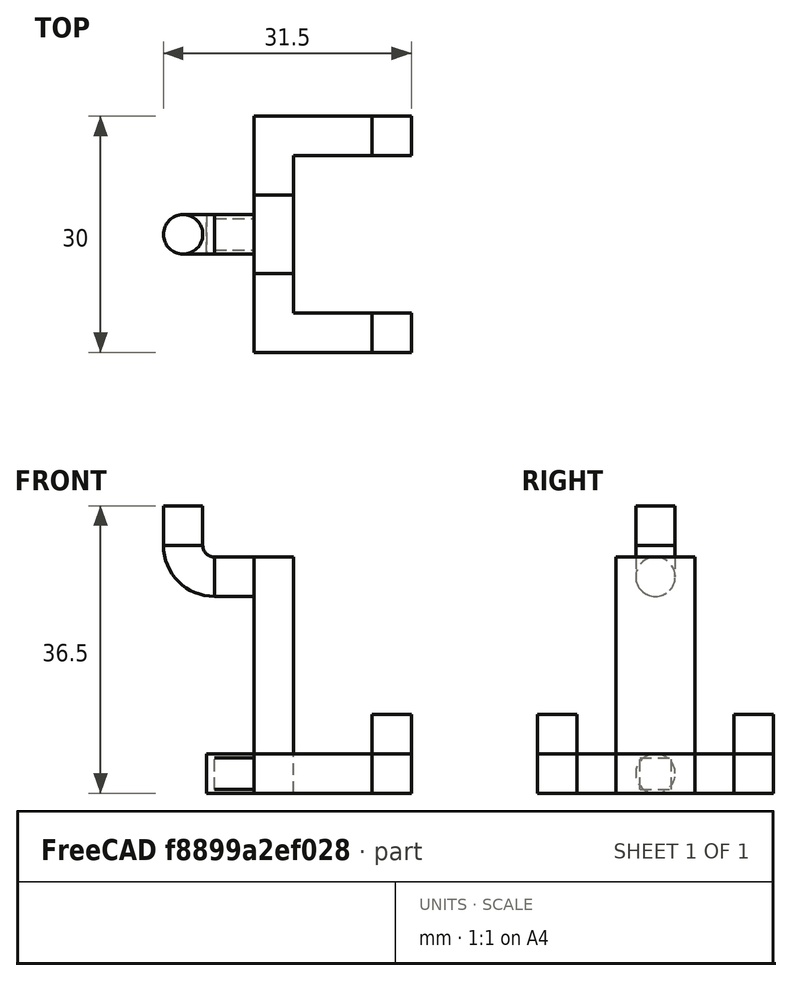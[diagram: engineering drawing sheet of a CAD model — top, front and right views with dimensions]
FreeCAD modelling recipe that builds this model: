
FCSTD DOCUMENT  (FreeCAD 0.17R13522 (Git))
Label: bigscrewdriver
License: All rights reserved
LicenseURL: http://en.wikipedia.org/wiki/All_rights_reserved
objects: Part::Box×6, Part::Cylinder×3, Part::Torus×1, Part::Cut×1
note: 11 computed .brp shape members not serialized (recipe doc carries the construction recipe); baked Part::Feature solids carry a one-line shape summary decoded from their .brp

FEATURE [Part::Cylinder] Cylinder002
  Angle = 360
  AttacherType = Attacher::AttachEngine3D
  Height = 6
  Placement = pos=(-5,0,2.5) rot=(0,-1,0;1.5708rad)
  Radius = 2.5
FEATURE [Part::Box] Box001  label="Cube001"
  AttacherType = Attacher::AttachEngine3D
  Height = 30
  Length = 5
  Placement = pos=(-5,-5,0) rot=(0,0,1;0rad)
  Width = 10
FEATURE [Part::Cylinder] Cylinder003
  Angle = 360
  AttacherType = Attacher::AttachEngine3D
  Height = 5
  Placement = pos=(-5,0,27.5) rot=(0,-1,0;1.5708rad)
  Radius = 2.5
FEATURE [Part::Torus] Torus
  Angle1 = -180
  Angle2 = 180
  Angle3 = 90
  AttacherType = Attacher::AttachEngine3D
  Placement = pos=(-10,0,31.5) rot=(0.57735,-0.57735,-0.57735;4.18879rad)
  Radius1 = 4
  Radius2 = 2.5
FEATURE [Part::Cylinder] Cylinder004
  Angle = 360
  AttacherType = Attacher::AttachEngine3D
  Height = 5
  Placement = pos=(-14,0,31.5) rot=(0,0,1;0rad)
  Radius = 2.5
FEATURE [Part::Box] Box002  label="Cube002"
  AttacherType = Attacher::AttachEngine3D
  Height = 4
  Length = 5
  Placement = pos=(-10,-2,0.5) rot=(0,0,1;0rad)
  Width = 4
FEATURE [Part::Box] Box  label="Cube"
  AttacherType = Attacher::AttachEngine3D
  Height = 5
  Length = 20
  Placement = pos=(-5,-15,0) rot=(0,0,1;0rad)
  Width = 30
FEATURE [Part::Box] Box003  label="Cube003"
  AttacherType = Attacher::AttachEngine3D
  Height = 10
  Length = 15
  Placement = pos=(0,-10,0) rot=(0,0,1;0rad)
  Width = 20
FEATURE [Part::Cut] Cut
  Base = -> Box
  Tool = -> Box003
FEATURE [Part::Box] Box004  label="Cube004"
  AttacherType = Attacher::AttachEngine3D
  Height = 10
  Length = 5
  Placement = pos=(10,10,0) rot=(0,0,1;0rad)
  Width = 5
FEATURE [Part::Box] Box005  label="Cube005"
  AttacherType = Attacher::AttachEngine3D
  Height = 10
  Length = 5
  Placement = pos=(10,-15,0) rot=(0,0,1;0rad)
  Width = 5
